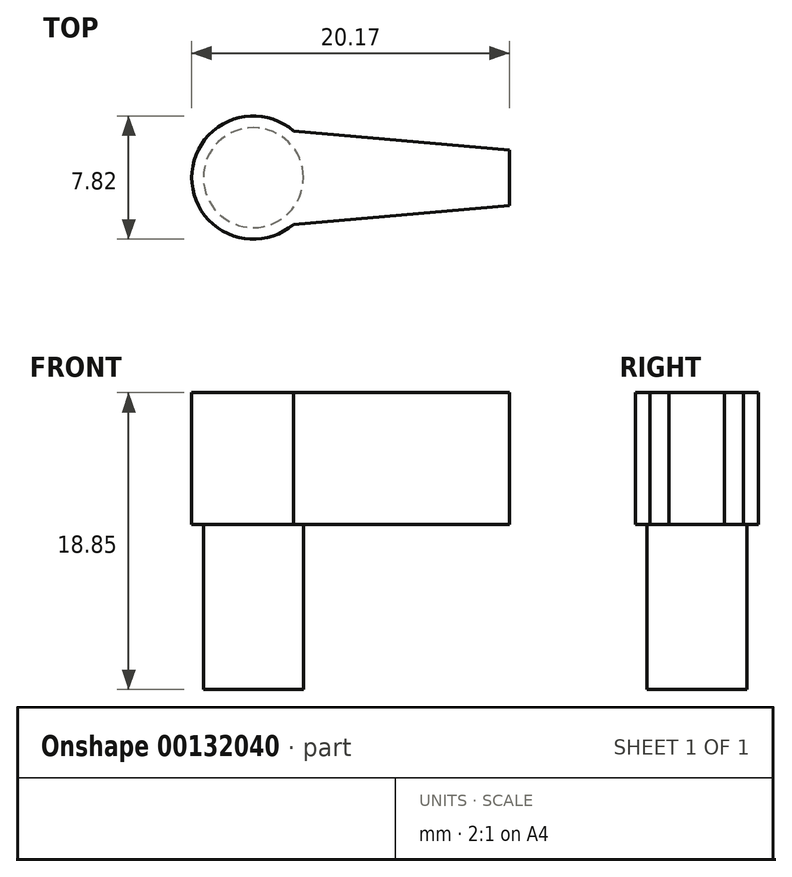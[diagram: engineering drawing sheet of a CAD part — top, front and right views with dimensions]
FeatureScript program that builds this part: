
annotation { "Feature Type Name" : "Feature", "Feature Type Description" : "" }
export const myFeature = defineFeature(function(context is Context, id is Id, definition is map)
    precondition{}
    {
        {
            var Q0;
            Q0=qCreatedBy(makeId("Top.planeOp"),FACE);
            var sketch = newSketch(context, id + "F0", { "sketchPlane" : qUnion([Q0])});
            skCircle(sketch, "E0", {"center": v(0, 0) * mm, "radius": 3.18 * mm});
            skSolve(sketch);
        }
        {
            var Q0;
            Q0 = qSketchRegion(id + "F0", true);
            extrude(context, id + "F1", {"entities" : qUnion([Q0]), "depth" : 10.46 * mm});
        }
        {
            var Q0;
            Q0=makeQuery(id+"F1.opExtrude","CAP_FACE",FACE,{"disambiguationData":[OSD([sQuery(id+"F0.wireOp",EDGE,"E0")])],"isStart":false});
            var sketch = newSketch(context, id + "F2", { "sketchPlane" : qUnion([Q0])});
            skArc(sketch, "E1", {"start": v(2.56, 2.96) * mm, "mid": v(-3.91, 0) * mm, "end": v(2.55, -2.97) * mm});
            skLineSegment(sketch, "E2", {"start": v(16.26, 1.75) * mm, "end": v(16.26, -1.78) * mm, "construction": true});
            skLineSegment(sketch, "E3", {"start": v(16.26, 0) * mm, "end": v(16.26, 1.75) * mm});
            skLineSegment(sketch, "E4", {"start": v(16.26, 0) * mm, "end": v(16.26, -1.78) * mm});
            skLineSegment(sketch, "E5", {"start": v(16.26, -1.78) * mm, "end": v(2.55, -2.97) * mm});
            skLineSegment(sketch, "E6", {"start": v(16.26, 1.75) * mm, "end": v(2.56, 2.96) * mm});
            skSolve(sketch);
        }
        {
            var Q0;
            Q0 = qSketchRegion(id + "F2", true);
            extrude(context, id + "F3", {"entities" : qUnion([Q0]), "operationType" : NewBodyOperationType.ADD, "depth" : 8.38 * mm});
        }
    });
